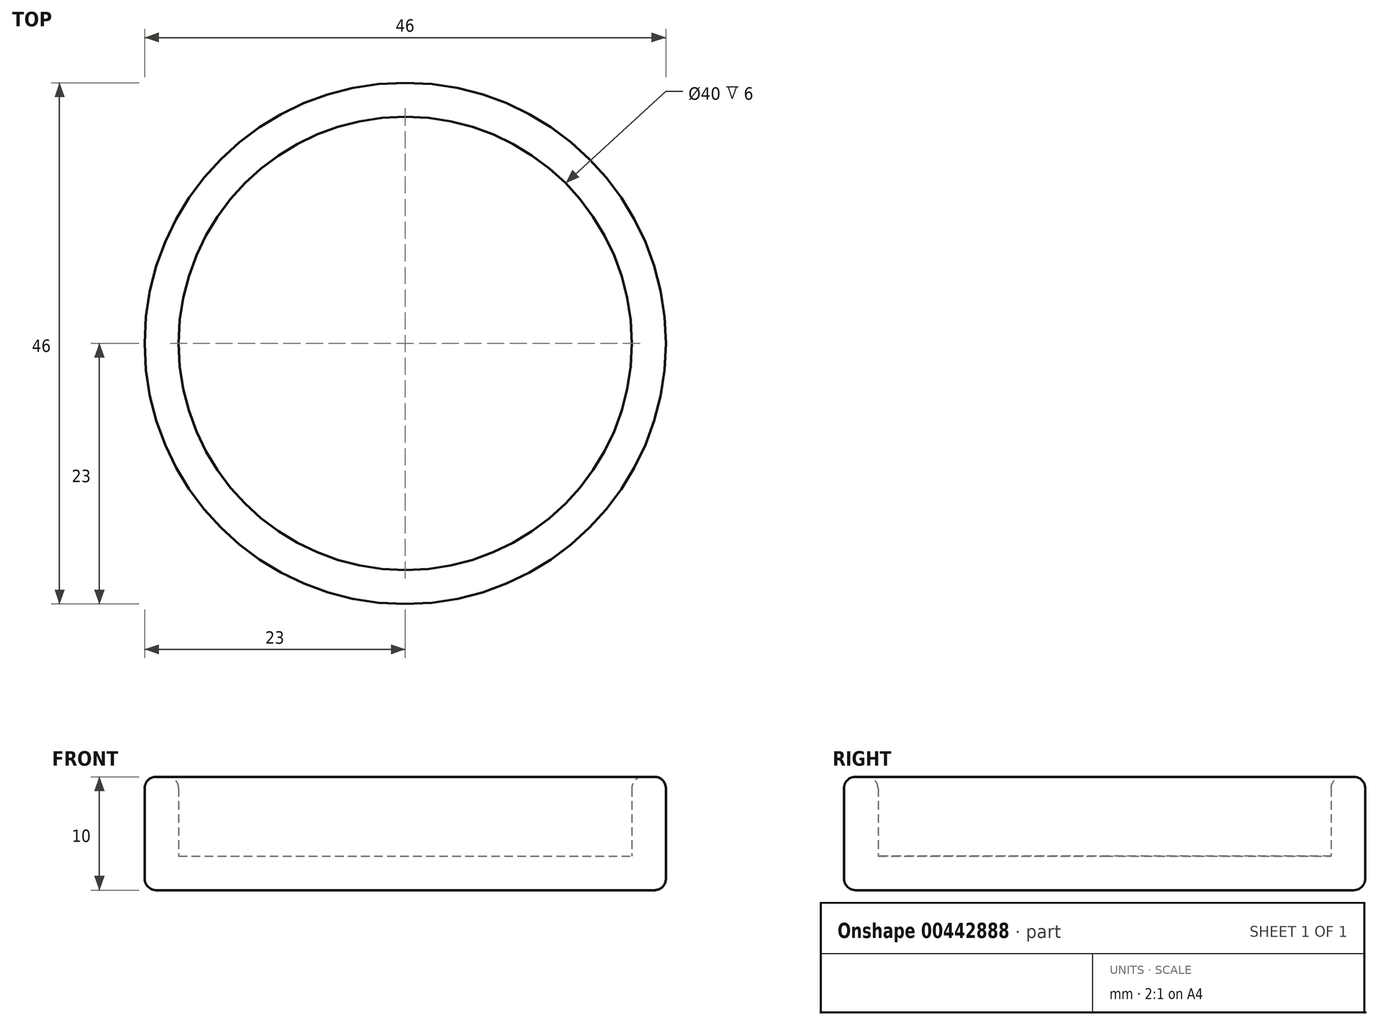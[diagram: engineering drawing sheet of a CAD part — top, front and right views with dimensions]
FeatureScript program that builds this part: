
annotation { "Feature Type Name" : "Feature", "Feature Type Description" : "" }
export const myFeature = defineFeature(function(context is Context, id is Id, definition is map)
    precondition{}
    {
        {
            var Q0;
            Q0=qCreatedBy(makeId("Top.planeOp"),FACE);
            var sketch = newSketch(context, id + "F0", { "sketchPlane" : qUnion([Q0])});
            skCircle(sketch, "E0", {"center": v(0, 0) * mm, "radius": 20 * mm});
            skCircle(sketch, "E1", {"center": v(0, 0) * mm, "radius": 23 * mm});
            skSolve(sketch);
        }
        {
            var Q0;
            Q0=makeQuery(id+"F0.imprint","IMPRINT",FACE,{"disambiguationData":[TD([[makeQuery(id+"F0.imprint","IMPRINT",EDGE,{"derivedFrom":sQuery(id+"F0.wireOp",EDGE,"E0")}),-1.0]])]});
            extrude(context, id + "F1", {"entities" : qUnion([Q0]), "depth" : 10 * mm});
        }
        {
            var Q0;
            Q0=makeQuery(id+"F1.opExtrude","CAP_FACE",FACE,{"disambiguationData":[OSD([sQuery(id+"F0.wireOp",EDGE,"E0"),sQuery(id+"F0.wireOp",EDGE,"E1")])],"isStart":true});
            var sketch = newSketch(context, id + "F2", { "sketchPlane" : qUnion([Q0])});
            skCircle(sketch, "E2", {"center": v(0, 0) * mm, "radius": 23 * mm});
            skSolve(sketch);
        }
        {
            var Q0;
            Q0 = qSketchRegion(id + "F2", true);
            extrude(context, id + "F3", {"entities" : qUnion([Q0]), "operationType" : NewBodyOperationType.ADD, "depth" : -3 * mm});
        }
        {
            var Q0;
            Q0=makeQuery(id+"F1.opExtrude","CAP_EDGE",EDGE,{"disambiguationData":[OSD([sQuery(id+"F0.wireOp",EDGE,"E1")])],"isStart":false});
            fillet(context, id + "F4", {"entities" : qUnion([Q0]), "radius" : 1 * mm, "tangentPropagation" : true, "allowEdgeOverflow" : false});
        }
        {
            var Q0;
            Q0=makeQuery(id+"F1.opExtrude","CAP_EDGE",EDGE,{"disambiguationData":[OSD([sQuery(id+"F0.wireOp",EDGE,"E0")])],"isStart":false});
            fillet(context, id + "F5", {"entities" : qUnion([Q0]), "radius" : 1 * mm, "tangentPropagation" : true, "allowEdgeOverflow" : false});
        }
        {
            var Q0;
            Q0=makeQuery(id+"F1.opExtrude","CAP_EDGE",EDGE,{"disambiguationData":[OSD([sQuery(id+"F0.wireOp",EDGE,"E1")])],"isStart":true});
            fillet(context, id + "F6", {"entities" : qUnion([Q0]), "radius" : 1 * mm, "tangentPropagation" : true, "allowEdgeOverflow" : false});
        }
    });
